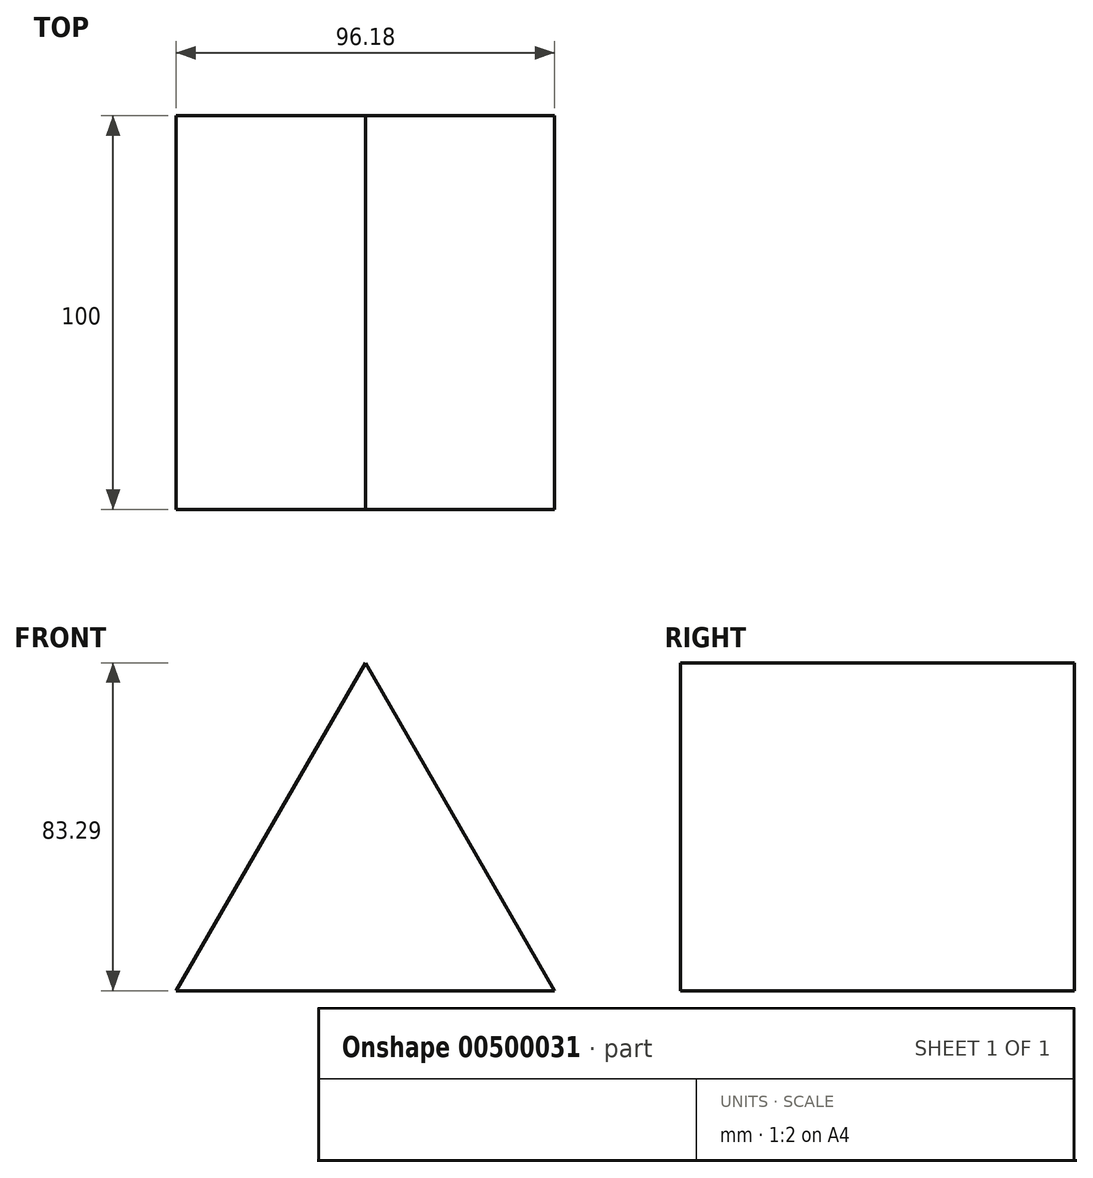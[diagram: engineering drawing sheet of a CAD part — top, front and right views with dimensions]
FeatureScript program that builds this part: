
annotation { "Feature Type Name" : "Feature", "Feature Type Description" : "" }
export const myFeature = defineFeature(function(context is Context, id is Id, definition is map)
    precondition{}
    {
        {
            var Q0;
            Q0=qCreatedBy(makeId("Front.planeOp"),FACE);
            var sketch = newSketch(context, id + "F0", { "sketchPlane" : qUnion([Q0])});
            skCircle(sketch, "E0.cCircle", {"center": v(0, 0) * mm, "radius": 55.53 * mm, "construction": true});
            skLineSegment(sketch, "E0.0", {"start": v(0, 55.53) * mm, "end": v(48.09, -27.76) * mm});
            skLineSegment(sketch, "E0.1", {"start": v(48.09, -27.76) * mm, "end": v(-48.09, -27.76) * mm});
            skLineSegment(sketch, "E0.2", {"start": v(-48.09, -27.76) * mm, "end": v(0, 55.53) * mm});
            skSolve(sketch);
        }
        {
            var Q0;
            Q0 = qSketchRegion(id + "F0", true);
            extrude(context, id + "F1", {"entities" : qUnion([Q0]), "endBound" : BoundingType.SYMMETRIC, "depth" : 100 * mm});
        }
    });
